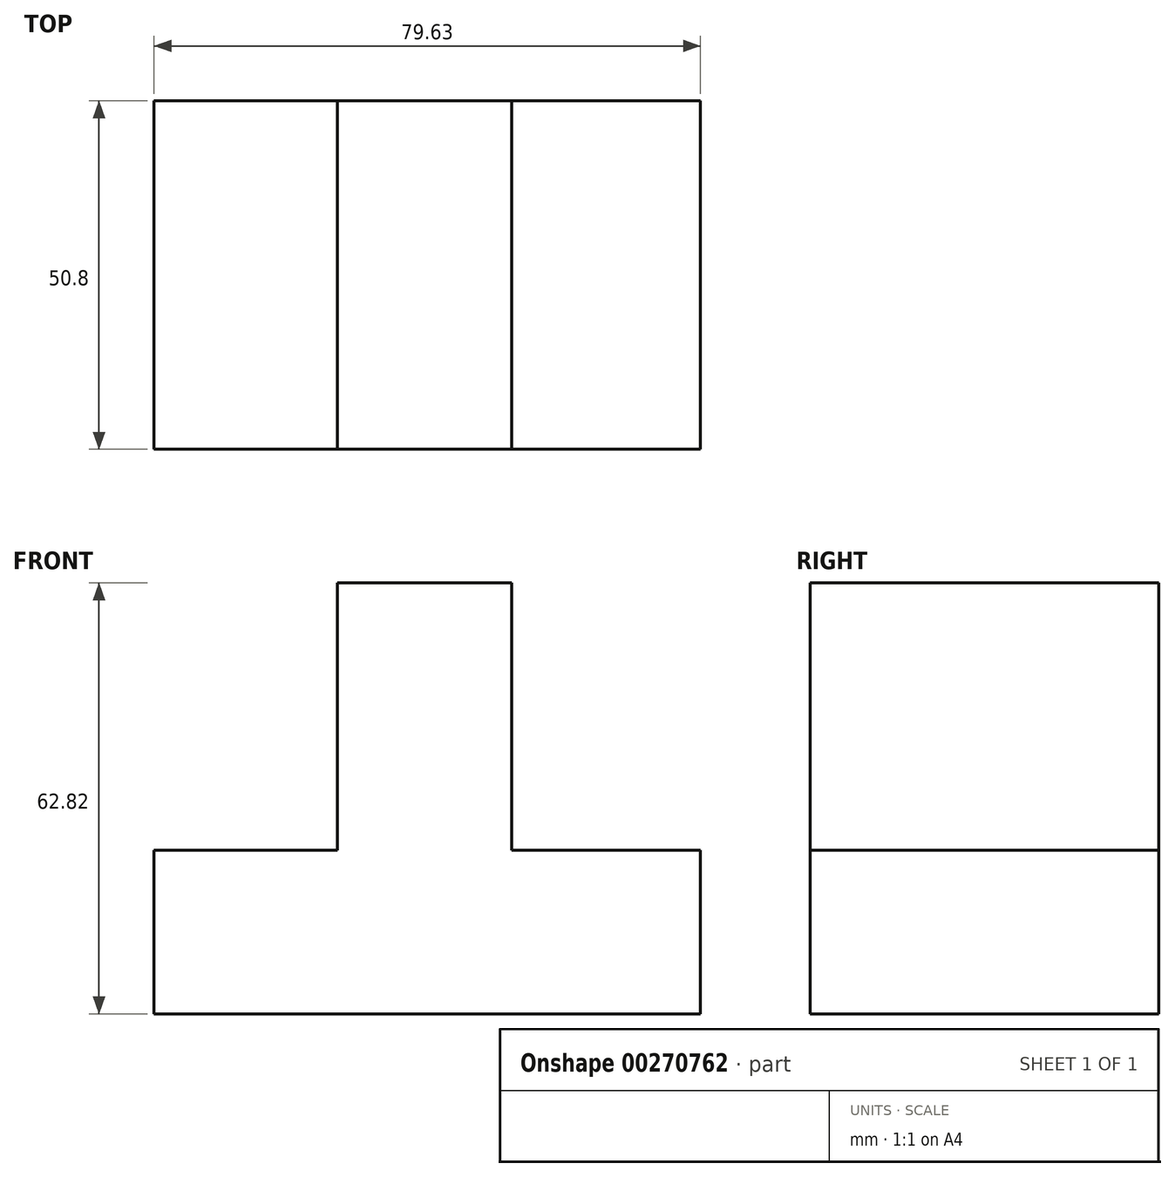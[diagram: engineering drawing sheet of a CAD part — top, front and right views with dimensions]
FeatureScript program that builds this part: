
annotation { "Feature Type Name" : "Feature", "Feature Type Description" : "" }
export const myFeature = defineFeature(function(context is Context, id is Id, definition is map)
    precondition{}
    {
        {
            var Q0;
            Q0=qCreatedBy(makeId("Front.planeOp"),FACE);
            var sketch = newSketch(context, id + "F0", { "sketchPlane" : qUnion([Q0])});
            skLineSegment(sketch, "E0", {"start": v(-76.1, 0) * mm, "end": v(-76.1, 23.87) * mm});
            skLineSegment(sketch, "E1", {"start": v(-76.1, 23.87) * mm, "end": v(-49.36, 23.87) * mm});
            skLineSegment(sketch, "E2", {"start": v(-49.36, 23.87) * mm, "end": v(-49.36, 62.82) * mm});
            skLineSegment(sketch, "E3", {"start": v(-49.36, 62.82) * mm, "end": v(-23.96, 62.82) * mm});
            skLineSegment(sketch, "E4", {"start": v(-23.96, 62.82) * mm, "end": v(-23.96, 23.87) * mm});
            skLineSegment(sketch, "E5", {"start": v(-23.96, 23.87) * mm, "end": v(3.53, 23.87) * mm});
            skLineSegment(sketch, "E6", {"start": v(3.53, 23.87) * mm, "end": v(3.53, 0) * mm});
            skLineSegment(sketch, "E7", {"start": v(3.53, 0) * mm, "end": v(-76.1, 0) * mm});
            skSolve(sketch);
        }
        {
            var Q0;
            Q0=makeQuery(id+"F0.imprint","IMPRINT",FACE,{"disambiguationData":[TD([[makeQuery(id+"F0.imprint","IMPRINT",EDGE,{"derivedFrom":sQuery(id+"F0.wireOp",EDGE,"E0")}),-1.0]])]});
            extrude(context, id + "F1", {"entities" : qUnion([Q0]), "depth" : 50.8 * mm});
        }
    });
